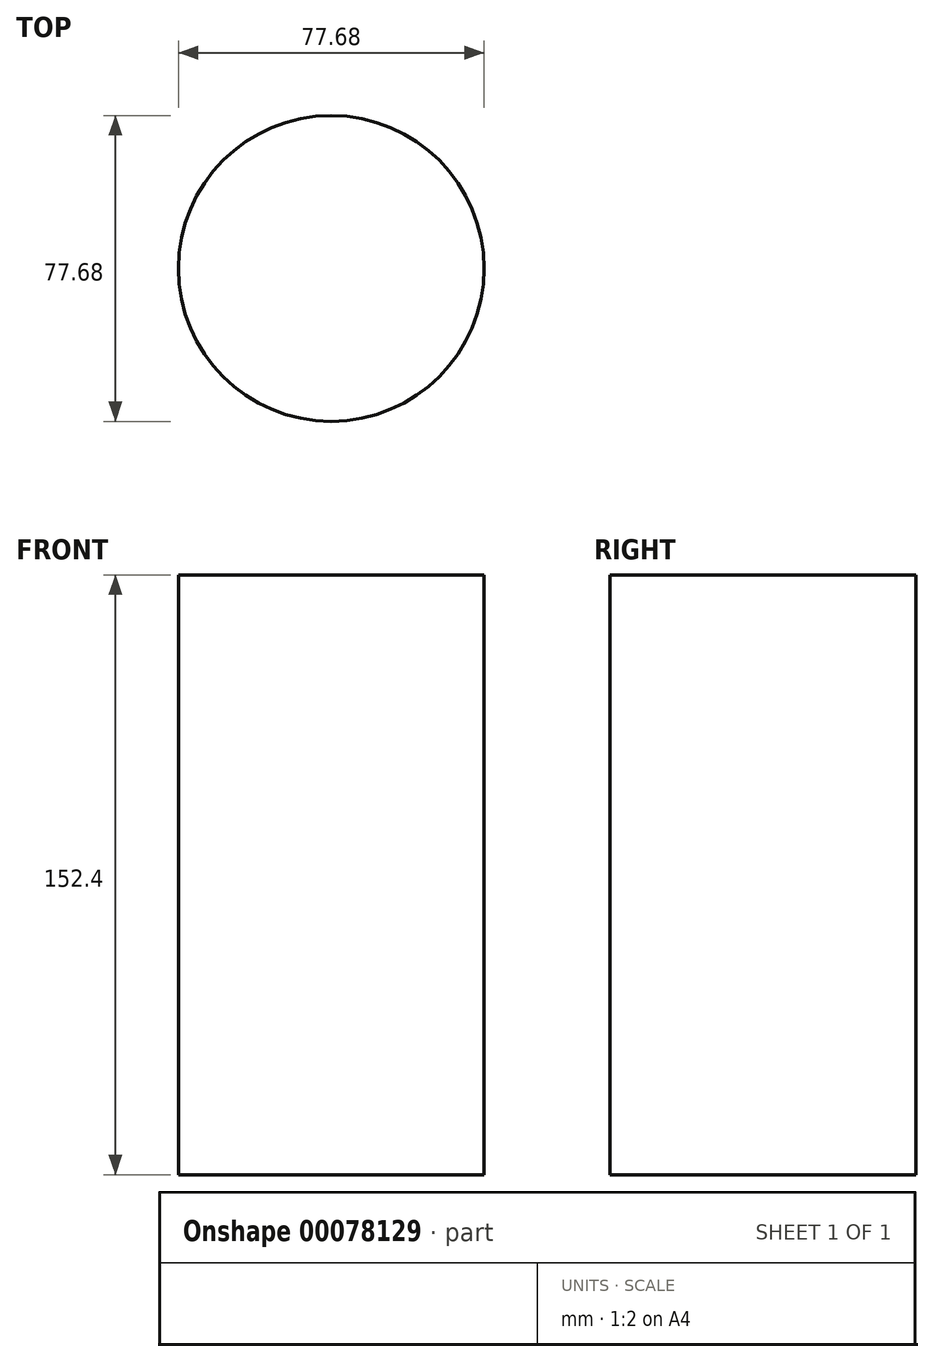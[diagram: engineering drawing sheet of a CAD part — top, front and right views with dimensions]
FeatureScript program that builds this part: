
annotation { "Feature Type Name" : "Feature", "Feature Type Description" : "" }
export const myFeature = defineFeature(function(context is Context, id is Id, definition is map)
    precondition{}
    {
        {
            var Q0;
            Q0=qCreatedBy(makeId("Top.planeOp"),FACE);
            var sketch = newSketch(context, id + "F0", { "sketchPlane" : qUnion([Q0])});
            skCircle(sketch, "E0", {"center": v(0, 0) * mm, "radius": 38.84 * mm});
            skSolve(sketch);
        }
        {
            var Q0;
            Q0=makeQuery(id+"F0.imprint","IMPRINT",FACE,{"disambiguationData":[TD([[makeQuery(id+"F0.imprint","IMPRINT",EDGE,{"derivedFrom":sQuery(id+"F0.wireOp",EDGE,"E0")}),1.0]])]});
            extrude(context, id + "F1", {"entities" : qUnion([Q0]), "depth" : 152.4 * mm});
        }
    });
